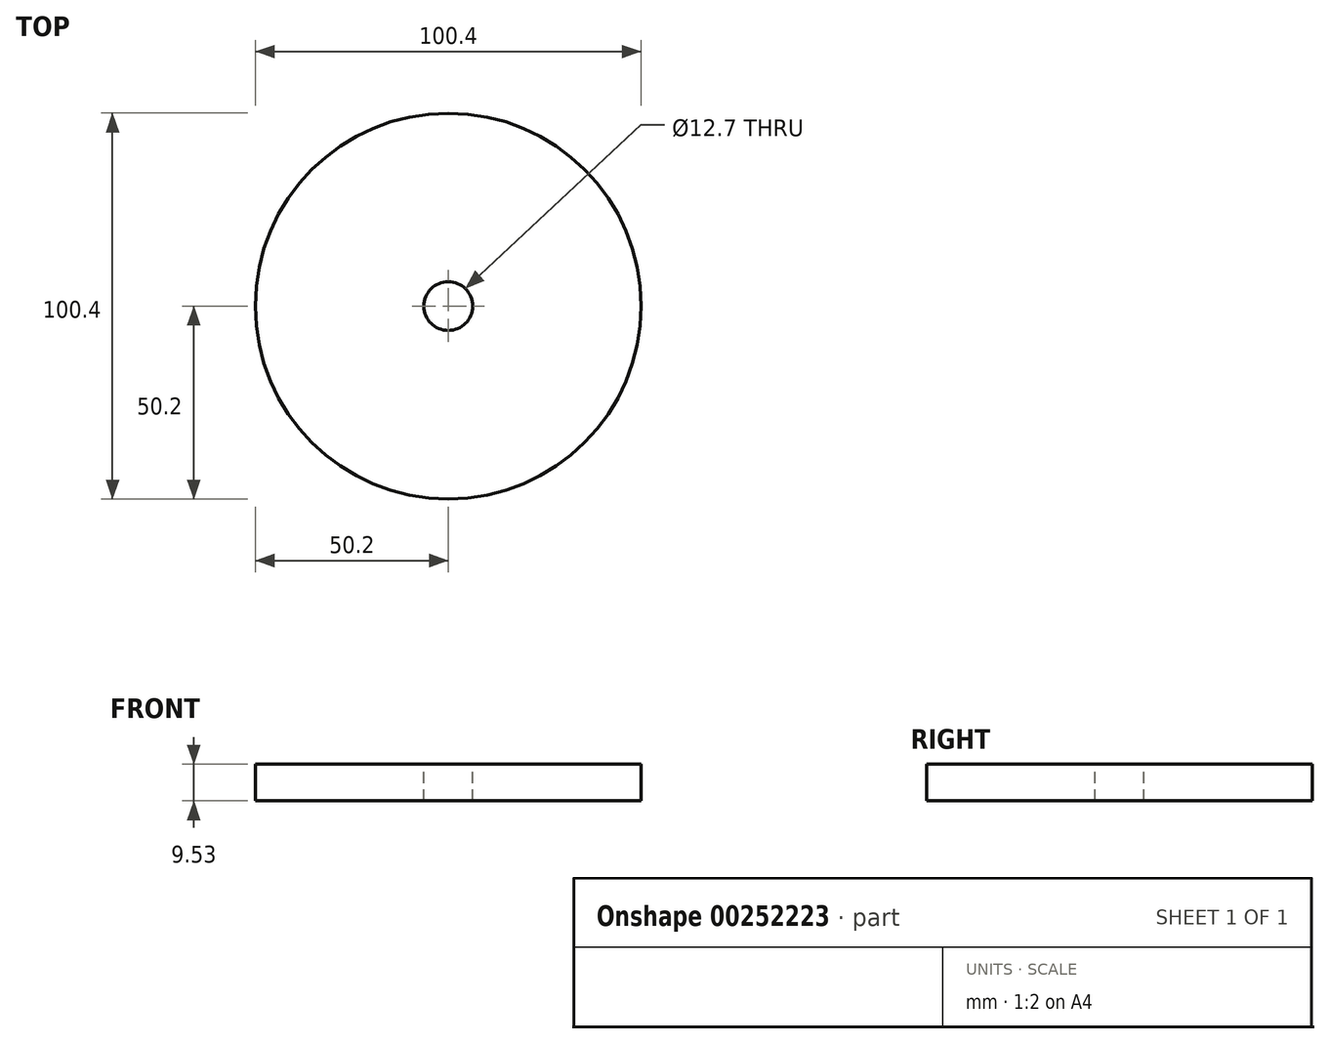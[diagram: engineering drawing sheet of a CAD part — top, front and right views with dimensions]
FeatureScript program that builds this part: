
annotation { "Feature Type Name" : "Feature", "Feature Type Description" : "" }
export const myFeature = defineFeature(function(context is Context, id is Id, definition is map)
    precondition{}
    {
        {
            var Q0;
            Q0=qCreatedBy(makeId("Top.planeOp"),FACE);
            var sketch = newSketch(context, id + "F0", { "sketchPlane" : qUnion([Q0])});
            skCircle(sketch, "E0", {"center": v(0, 0) * mm, "radius": 50.2 * mm});
            skLineSegment(sketch, "E1", {"start": v(0, 0) * mm, "end": v(31.66, -38.95) * mm});
            skLineSegment(sketch, "E2", {"start": v(31.66, -38.95) * mm, "end": v(0, 0) * mm});
            skSolve(sketch);
        }
        {
            var Q0;
            Q0=makeQuery(id+"F0.imprint","IMPRINT",FACE,{"disambiguationData":[TD([[makeQuery(id+"F0.imprint","IMPRINT",EDGE,{"derivedFrom":sQuery(id+"F0.wireOp",EDGE,"E0")}),1.0]])]});
            extrude(context, id + "F1", {"entities" : qUnion([Q0]), "depth" : 9.52 * mm});
        }
        {
            var Q0;
            Q0=makeQuery(id+"F1.opExtrude","CAP_FACE",FACE,{"disambiguationData":[OSD([sQuery(id+"F0.wireOp",EDGE,"E0")])],"isStart":false});
            var sketch = newSketch(context, id + "F2", { "sketchPlane" : qUnion([Q0])});
            skLineSegment(sketch, "E3", {"start": v(0, 0) * mm, "end": v(30.89, -39.57) * mm});
            skSolve(sketch);
        }
        {
            var Q0;
            Q0=sQuery(id+"F2.wireOp",VERTEX,"E3.start");
            var Q1;
            Q1=makeQuery(id+"F1.opExtrude","SWEPT_BODY",BODY,{"disambiguationData":[OSD([sQuery(id+"F0.wireOp",EDGE,"E0")])]});
            hole(context, id + "F3", {"style" : HoleStyle.SIMPLE, "endStyle" : HoleEndStyle.THROUGH, "holeDiameter" : 12.7 * mm, "tappedDepth" : 12.7 * mm, "tapClearance" : 3, "locations" : qUnion([Q0]), "scope" : qUnion([Q1])});
        }
    });
